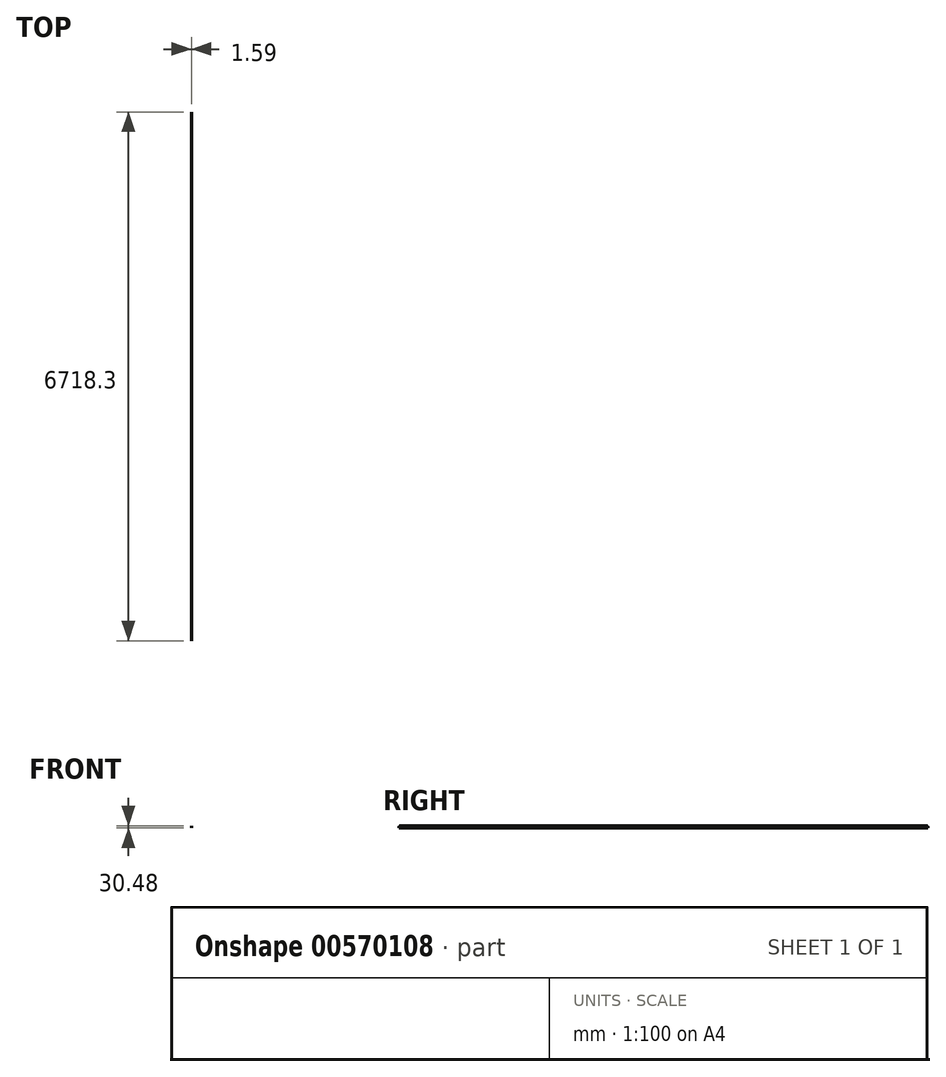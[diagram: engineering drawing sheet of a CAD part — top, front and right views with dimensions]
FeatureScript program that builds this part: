
annotation { "Feature Type Name" : "Feature", "Feature Type Description" : "" }
export const myFeature = defineFeature(function(context is Context, id is Id, definition is map)
    precondition{}
    {
        {
            var Q0;
            Q0=qCreatedBy(makeId("Front.planeOp"),FACE);
            var sketch = newSketch(context, id + "F0", { "sketchPlane" : qUnion([Q0])});
            skLineSegment(sketch, "E0.bottom", {"start": v(0, 0) * mm, "end": v(1.59, 0) * mm});
            skLineSegment(sketch, "E0.top", {"start": v(0, -30.48) * mm, "end": v(1.59, -30.48) * mm});
            skLineSegment(sketch, "E0.left", {"start": v(0, 0) * mm, "end": v(0, -30.48) * mm});
            skLineSegment(sketch, "E0.right", {"start": v(1.59, 0) * mm, "end": v(1.59, -30.48) * mm});
            skSolve(sketch);
        }
        {
            var Q0;
            Q0=qSketchRegion(id+"F0",true);
            extrude(context, id + "F1", {"entities" : qUnion([Q0]), "depth" : 6718.3 * mm, "offsetDistance" : 25.4 * mm});
        }
        {
            var Q0;
            Q0=makeQuery(id+"F1.opExtrude","SWEPT_FACE",FACE,{"disambiguationData":[OSD([sQuery(id+"F0.wireOp",EDGE,"E0.bottom")])]});
            var sketch = newSketch(context, id + "F2", { "sketchPlane" : qUnion([Q0])});
            skLineSegment(sketch, "E1.0", {"start": v(0, -7.14) * mm, "end": v(1.59, -7.14) * mm});
            skLineSegment(sketch, "E2.0", {"start": v(0, -6711.16) * mm, "end": v(1.59, -6711.16) * mm});
            skSolve(sketch);
        }
        {
            var Q0;
            {var subQ0=sQuery(id+"F2.wireOp",EDGE,"E2.0");Q0=makeQuery(id+"F2.imprint","IMPRINT",FACE,{"disambiguationData":[TD([[makeQuery(id+"F2.imprint","IMPRINT",EDGE,{"derivedFrom":subQ0}),-1.0]])]});}
            var Q1;
            {var subQ0=sQuery(id+"F2.wireOp",EDGE,"E1.0");Q1=makeQuery(id+"F2.imprint","IMPRINT",FACE,{"disambiguationData":[TD([[makeQuery(id+"F2.imprint","IMPRINT",EDGE,{"derivedFrom":subQ0}),1.0]])]});}
            extrude(context, id + "F3", {"entities" : qUnion([Q0, Q1]), "operationType" : NewBodyOperationType.REMOVE, "oppositeDirection" : true, "depth" : 6.35 * mm, "offsetDistance" : 25.4 * mm});
        }
    });
